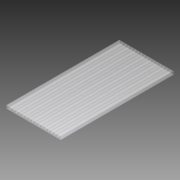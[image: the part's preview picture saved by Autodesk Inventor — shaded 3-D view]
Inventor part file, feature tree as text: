
AUTODESK INVENTOR PART (.ipt)
format: ipt  version: 2012 (Build 160160000, 160)  size: 156,160 bytes
history: native  units: in
note: dims shown in document units (in); Inventor stores cm internally (conversion verified against a paired STEP export)
features: extrude x1, sketch x1
ambient origin geometry x8: Origin, YZ Plane, XZ Plane, XY Plane, X Axis, Y Axis, Z Axis, Center Point
bodies: Solid1 (feature_tree)
feature tree (2):
  extrude  "Extrusion1"  Depth=0.25in
  sketch  "Sketch1"  dims[d0=4.27in d1=0.25in d2=0.0201in d3=0.02in d4=0.02in d5=0.23in d6=6.6929in d8=0.25in d9=0.3937in d11=1.0in d13=8.875in d14=0.0in]
